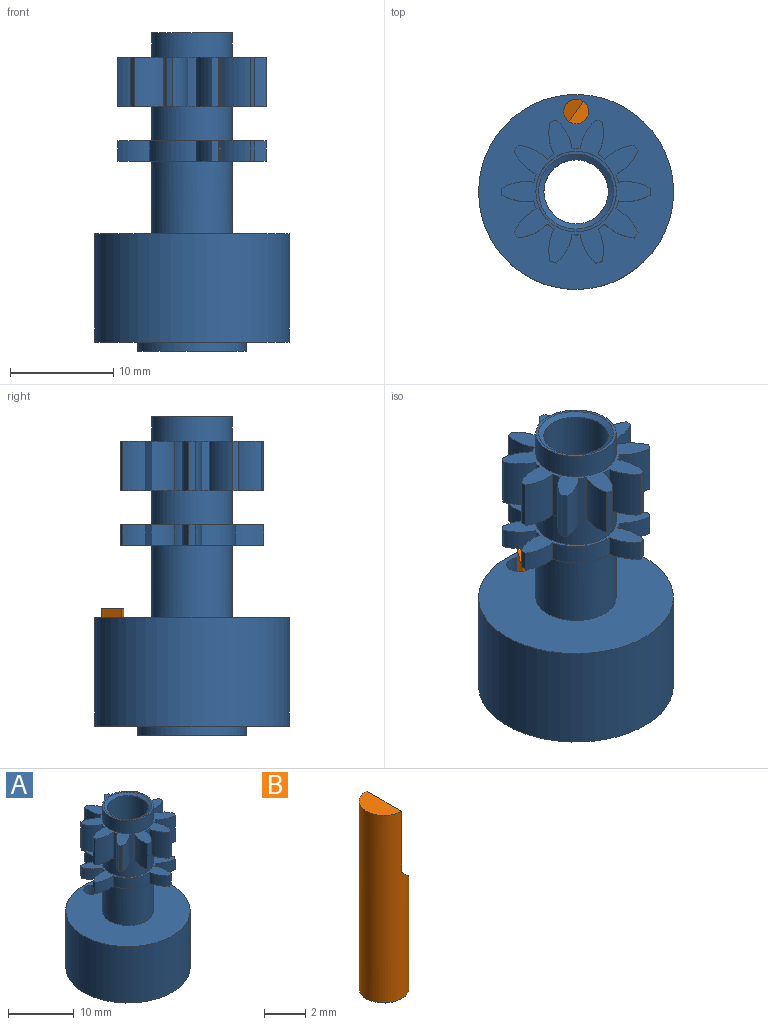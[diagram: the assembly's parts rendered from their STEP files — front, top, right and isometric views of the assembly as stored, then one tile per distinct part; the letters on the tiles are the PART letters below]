
ASSEMBLY  parts=2 mates=1
PART A: 89 faces, bbox 18.9x18.9x30.9 mm
  f0: cylinder r=3.9mm len=7.8mm, axis (0,0,-1), area 58.8mm2, adj f9,f87
  f1: cylinder r=3.9mm len=7.8mm, axis (0,0,-1), area 80.9mm2, adj f13,f88
  f2: cone r=3.12mm half-angle=30deg, axis (0,0,-1), area 49.7mm2, adj f3,f10
  f3: plane 10.5x10.5mm, normal (0,0,-1), area 31.2mm2, adj f2,f4
  f4: cylinder r=5.25mm len=10.5mm, axis (0,0,-1), area 29.7mm2, adj f3,f5
  f5: plane 18.9x18.9mm, normal (0,0,-1), area 189.4mm2, adj f4,f6,f11
  f6: cylinder r=9.45mm len=18.9mm, axis (0,0,-1), area 623.4mm2, adj f5,f7
  f7: plane 18.9x18.9mm, normal (0,0,1), area 228.2mm2, adj f6,f8,f11
  f8: cylinder r=3.9mm len=7.8mm, axis (0,0,-1), area 172.8mm2, adj f7,f14
  f9: plane 7.8x7.8mm, normal (0,0,1), area 6.2mm2, adj f0,f12
  f10: cylinder r=3.12mm len=28.73mm, axis (0,0,-1), area 563.2mm2, adj f2,f12
  f11: cylinder r=1.2mm len=10.5mm, axis (0,0,1), area 79.2mm2, adj f5,f7
  f12: cone r=3.64mm half-angle=60deg, axis (0,0,1), area 12.7mm2, adj f9,f10
  f13: plane 14.4x13.88mm, normal (0,0,1), area 46.7mm2, adj f1,f15,f16,f17,f18,f19,f20,f21
  f14: plane 14.4x13.88mm, normal (0,0,-1), area 46.7mm2, adj f8,f15,f16,f17,f18,f19,f20,f21
  f15: cylinder r=4.2mm len=1.95mm, axis (0,0,-1), area 1.6mm2, adj f13,f14,f16,f17
  f16: cylinder r=4.5mm len=2.3mm, axis (0,0,-1), area 6.3mm2, adj f13,f14,f15,f21
  f17: cylinder r=4.5mm len=3.09mm, axis (0,0,-1), area 6.3mm2, adj f13,f14,f15,f46
  f18: cylinder r=4.5mm len=2.85mm, axis (0,0,-1), area 6.3mm2, adj f13,f14,f19,f21
  f19: cylinder r=4.2mm len=1.95mm, axis (0,0,-1), area 1.6mm2, adj f13,f14,f18,f20
  f20: cylinder r=4.5mm len=3.12mm, axis (0,0,-1), area 6.3mm2, adj f13,f14,f19,f25
  f21: cylinder r=7.2mm len=1.95mm, axis (0,0,-1), area 1.2mm2, adj f13,f14,f16,f18
  f22: cylinder r=4.5mm len=2.76mm, axis (0,0,-1), area 6.3mm2, adj f13,f14,f23,f25
  f23: cylinder r=4.2mm len=1.95mm, axis (0,0,-1), area 1.6mm2, adj f13,f14,f22,f24
  f24: cylinder r=4.5mm len=2.76mm, axis (0,0,-1), area 6.3mm2, adj f13,f14,f23,f29
  f25: cylinder r=7.2mm len=1.95mm, axis (0,0,-1), area 1.2mm2, adj f13,f14,f20,f22
  f26: cylinder r=4.5mm len=3.12mm, axis (0,0,-1), area 6.3mm2, adj f13,f14,f27,f29
  f27: cylinder r=4.2mm len=1.95mm, axis (0,0,-1), area 1.6mm2, adj f13,f14,f26,f28
  f28: cylinder r=4.5mm len=2.85mm, axis (0,0,-1), area 6.3mm2, adj f13,f14,f27,f33
  f29: cylinder r=7.2mm len=1.95mm, axis (0,0,-1), area 1.2mm2, adj f13,f14,f24,f26
  f30: cylinder r=4.5mm len=2.3mm, axis (0,0,-1), area 6.3mm2, adj f13,f14,f31,f33
  f31: cylinder r=4.2mm len=1.95mm, axis (0,0,-1), area 1.6mm2, adj f13,f14,f30,f32
  f32: cylinder r=4.5mm len=3.09mm, axis (0,0,-1), area 6.3mm2, adj f13,f14,f31,f37
  f33: cylinder r=7.2mm len=1.95mm, axis (0,0,-1), area 1.2mm2, adj f13,f14,f28,f30
  f34: cylinder r=4.5mm len=3.09mm, axis (0,0,-1), area 6.3mm2, adj f13,f14,f35,f37
  f35: cylinder r=4.2mm len=1.95mm, axis (0,0,-1), area 1.6mm2, adj f13,f14,f34,f36
  f36: cylinder r=4.5mm len=2.3mm, axis (0,0,-1), area 6.3mm2, adj f13,f14,f35,f41
  f37: cylinder r=7.2mm len=1.95mm, axis (0,0,-1), area 1.2mm2, adj f13,f14,f32,f34
  f38: cylinder r=4.5mm len=2.85mm, axis (0,0,-1), area 6.3mm2, adj f13,f14,f39,f41
  f39: cylinder r=4.2mm len=1.95mm, axis (0,0,-1), area 1.6mm2, adj f13,f14,f38,f40
  f40: cylinder r=4.5mm len=3.12mm, axis (0,0,-1), area 6.3mm2, adj f13,f14,f39,f44
  f41: cylinder r=7.2mm len=1.95mm, axis (0,0,-1), area 1.2mm2, adj f13,f14,f36,f38
  f42: cylinder r=4.5mm len=2.76mm, axis (0,0,-1), area 6.3mm2, adj f13,f14,f43,f44
  f43: cylinder r=4.2mm len=4.5mm, axis (0,0,-1), area 11.9mm2, adj f13,f14,f42,f45
  f44: cylinder r=7.2mm len=1.95mm, axis (0,0,-1), area 1.2mm2, adj f13,f14,f40,f42
  f45: cylinder r=4.5mm len=3.09mm, axis (0,0,-1), area 6.3mm2, adj f13,f14,f43,f46
  f46: cylinder r=7.2mm len=1.95mm, axis (0,0,-1), area 1.2mm2, adj f13,f14,f17,f45
  f47: cylinder r=4.5mm len=4.8mm, axis (0,0,-1), area 15.4mm2, adj f48,f86,f87,f88
  f48: cylinder r=7.2mm len=4.8mm, axis (0,0,-1), area 3.1mm2, adj f47,f49,f87,f88
  f49: cylinder r=4.5mm len=4.8mm, axis (0,0,-1), area 15.4mm2, adj f48,f50,f87,f88
  f50: cylinder r=4.2mm len=4.8mm, axis (0,0,-1), area 3.9mm2, adj f49,f51,f87,f88
  f51: cylinder r=4.5mm len=4.8mm, axis (0,0,-1), area 15.4mm2, adj f50,f52,f87,f88
  f52: cylinder r=7.2mm len=4.8mm, axis (0,0,-1), area 3.1mm2, adj f51,f53,f87,f88
  f53: cylinder r=4.5mm len=4.8mm, axis (0,0,-1), area 15.4mm2, adj f52,f54,f87,f88
  f54: cylinder r=4.2mm len=4.8mm, axis (0,0,-1), area 3.9mm2, adj f53,f55,f87,f88
  f55: cylinder r=4.5mm len=4.8mm, axis (0,0,-1), area 15.4mm2, adj f54,f56,f87,f88
  f56: cylinder r=7.2mm len=4.8mm, axis (0,0,-1), area 3.1mm2, adj f55,f57,f87,f88
  f57: cylinder r=4.5mm len=4.8mm, axis (0,0,-1), area 15.4mm2, adj f56,f58,f87,f88
  f58: cylinder r=4.2mm len=4.8mm, axis (0,0,-1), area 3.9mm2, adj f57,f59,f87,f88
  f59: cylinder r=4.5mm len=4.8mm, axis (0,0,-1), area 15.4mm2, adj f58,f60,f87,f88
  f60: cylinder r=7.2mm len=4.8mm, axis (0,0,-1), area 3.1mm2, adj f59,f61,f87,f88
  f61: cylinder r=4.5mm len=4.8mm, axis (0,0,-1), area 15.4mm2, adj f60,f62,f87,f88
  f62: cylinder r=4.2mm len=4.8mm, axis (0,0,-1), area 3.9mm2, adj f61,f63,f87,f88
  f63: cylinder r=4.5mm len=4.8mm, axis (0,0,-1), area 15.4mm2, adj f62,f64,f87,f88
  f64: cylinder r=7.2mm len=4.8mm, axis (0,0,-1), area 3.1mm2, adj f63,f65,f87,f88
  f65: cylinder r=4.5mm len=4.8mm, axis (0,0,-1), area 15.4mm2, adj f64,f66,f87,f88
  f66: cylinder r=4.2mm len=4.8mm, axis (0,0,-1), area 3.9mm2, adj f65,f67,f87,f88
  f67: cylinder r=4.5mm len=4.8mm, axis (0,0,-1), area 15.4mm2, adj f66,f68,f87,f88
  f68: cylinder r=7.2mm len=4.8mm, axis (0,0,-1), area 3.1mm2, adj f67,f69,f87,f88
  f69: cylinder r=4.5mm len=4.8mm, axis (0,0,-1), area 15.4mm2, adj f68,f70,f87,f88
  f70: cylinder r=4.2mm len=4.8mm, axis (0,0,-1), area 3.9mm2, adj f69,f71,f87,f88
  f71: cylinder r=4.5mm len=4.8mm, axis (0,0,-1), area 15.4mm2, adj f70,f72,f87,f88
  f72: cylinder r=7.2mm len=4.8mm, axis (0,0,-1), area 3.1mm2, adj f71,f73,f87,f88
  f73: cylinder r=4.5mm len=4.8mm, axis (0,0,-1), area 15.4mm2, adj f72,f74,f87,f88
  f74: cylinder r=4.2mm len=4.8mm, axis (0,0,-1), area 3.9mm2, adj f73,f75,f87,f88
  f75: cylinder r=4.5mm len=4.8mm, axis (0,0,-1), area 15.4mm2, adj f74,f76,f87,f88
  f76: cylinder r=7.2mm len=4.8mm, axis (0,0,-1), area 3.1mm2, adj f75,f77,f87,f88
  f77: cylinder r=4.5mm len=4.8mm, axis (0,0,-1), area 15.4mm2, adj f76,f78,f87,f88
  f78: cylinder r=4.2mm len=4.8mm, axis (0,0,-1), area 3.9mm2, adj f77,f79,f87,f88
  f79: cylinder r=4.5mm len=4.8mm, axis (0,0,-1), area 15.4mm2, adj f78,f80,f87,f88
  f80: cylinder r=7.2mm len=4.8mm, axis (0,0,-1), area 3.1mm2, adj f79,f81,f87,f88
  f81: cylinder r=4.5mm len=4.8mm, axis (0,0,-1), area 15.4mm2, adj f80,f82,f87,f88
  f82: cylinder r=4.2mm len=4.8mm, axis (0,0,-1), area 3.9mm2, adj f81,f83,f87,f88
  f83: cylinder r=4.5mm len=4.8mm, axis (0,0,-1), area 15.4mm2, adj f82,f84,f87,f88
  f84: cylinder r=7.2mm len=4.8mm, axis (0,0,-1), area 3.1mm2, adj f83,f85,f87,f88
  f85: cylinder r=4.5mm len=4.8mm, axis (0,0,-1), area 15.4mm2, adj f84,f86,f87,f88
  f86: cylinder r=4.2mm len=4.8mm, axis (0,0,-1), area 3.9mm2, adj f47,f85,f87,f88
  f87: plane 14.4x13.88mm, normal (0,0,1), area 56.4mm2, adj f0,f47,f48,f49,f50,f51,f52,f53
  f88: plane 14.4x13.88mm, normal (0,0,-1), area 56.4mm2, adj f1,f47,f48,f49,f50,f51,f52,f53
PART B: 5 faces, bbox 2.4x2.4x11.1 mm
  f0: cylinder r=1.2mm len=11.1mm, axis (0,0,-1), area 67.2mm2, adj f1,f2,f3,f4
  f1: plane 2.4x1.2mm, normal (0,0,1), area 2.3mm2, adj f0,f3
  f2: plane 2.4x2.4mm, normal (0,0,-1), area 4.5mm2, adj f0
  f3: plane 3.6x2.4mm, normal (1,0,0), area 8.6mm2, adj f0,f1,f4
  f4: plane 2.4x1.2mm, normal (0.71,0,0.71), area 3.2mm2, adj f0,f3
PLACE A at identity fixed
PLACE B rot(axis=(0,0,1),144deg) t=(0,7.8,1.2)mm
MATE fastened B.f0 <-> A.f11  axis (0,0,-1) through (0,7.8,12.3)mm
